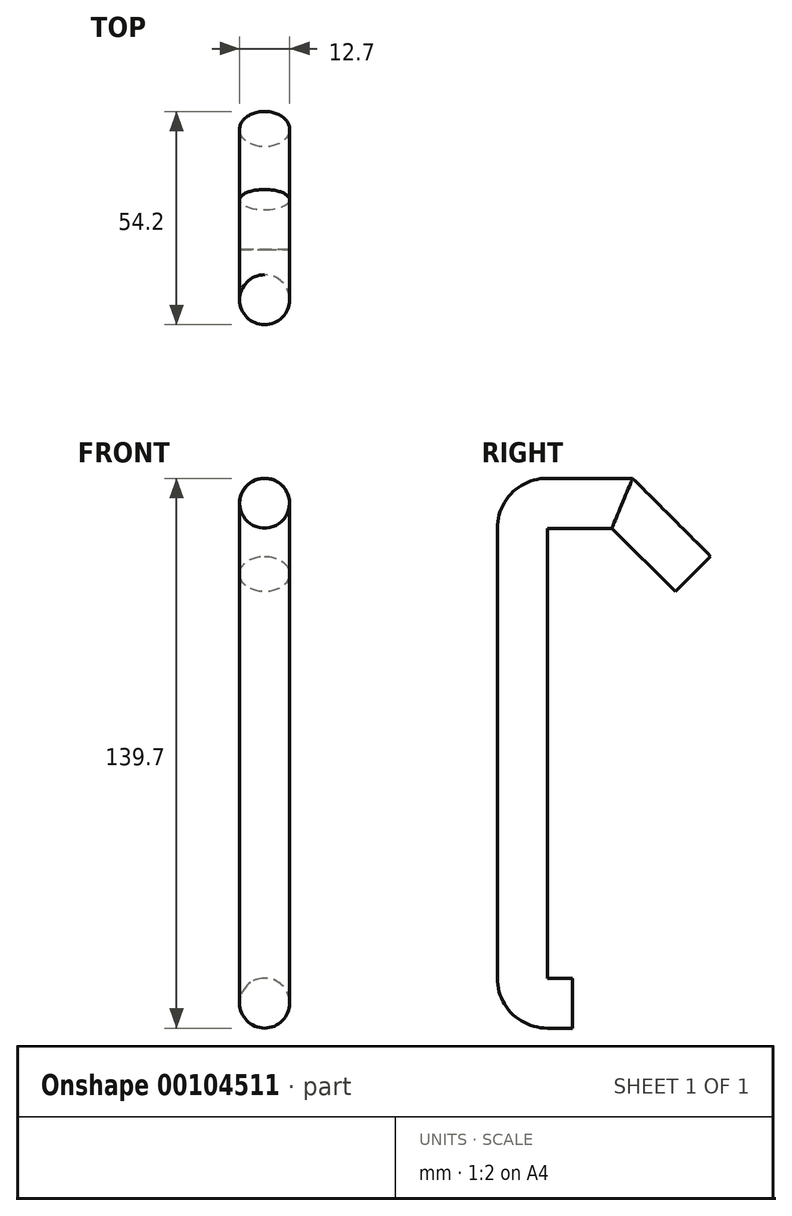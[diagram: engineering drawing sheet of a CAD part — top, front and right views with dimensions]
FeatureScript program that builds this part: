
annotation { "Feature Type Name" : "Feature", "Feature Type Description" : "" }
export const myFeature = defineFeature(function(context is Context, id is Id, definition is map)
    precondition{}
    {
        {
            var Q0;
            Q0=qCreatedBy(makeId("Front.planeOp"),FACE);
            var sketch = newSketch(context, id + "F0", { "sketchPlane" : qUnion([Q0])});
            skCircle(sketch, "E0", {"center": v(0, 0) * mm, "radius": 6.35 * mm});
            skSolve(sketch);
        }
        {
            var Q0;
            Q0=qCreatedBy(makeId("Right.planeOp"),FACE);
            var sketch = newSketch(context, id + "F1", { "sketchPlane" : qUnion([Q0])});
            skPoint(sketch, "E1", {"position": v(-12.7, 127) * mm});
            skPoint(sketch, "E2", {"position": v(0, 0) * mm});
            skPoint(sketch, "E3", {"position": v(-12.7, 0) * mm});
            skLineSegment(sketch, "E4", {"start": v(0, 0) * mm, "end": v(-6.35, 0) * mm});
            skLineSegment(sketch, "E5", {"start": v(-12.7, 120.65) * mm, "end": v(-12.7, 6.35) * mm});
            skArc(sketch, "E6.filletArc", {"start": v(-12.7, 6.35) * mm, "mid": v(-10.84, 1.86) * mm, "end": v(-6.35, 0) * mm});
            skPoint(sketch, "E7", {"position": v(12.7, 127) * mm});
            skLineSegment(sketch, "E8", {"start": v(12.7, 127) * mm, "end": v(-6.35, 127) * mm});
            skArc(sketch, "E9.filletArc", {"start": v(-6.35, 127) * mm, "mid": v(-10.84, 125.14) * mm, "end": v(-12.7, 120.65) * mm});
            skLineSegment(sketch, "E10", {"start": v(12.7, 127) * mm, "end": v(30.66, 109.04) * mm});
            skSolve(sketch);
        }
        {
            var Q0;
            Q0=makeQuery(id+"F0.imprint","IMPRINT",FACE,{"disambiguationData":[TD([[makeQuery(id+"F0.imprint","IMPRINT",EDGE,{"derivedFrom":sQuery(id+"F0.wireOp",EDGE,"E0")}),1.0]])]});
            var Q1;
            Q1=sQuery(id+"F1.wireOp",EDGE,"E4");
            var Q2;
            Q2=sQuery(id+"F1.wireOp",EDGE,"E6.filletArc");
            var Q3;
            Q3=sQuery(id+"F1.wireOp",EDGE,"E5");
            var Q4;
            Q4=sQuery(id+"F1.wireOp",EDGE,"E9.filletArc");
            var Q5;
            Q5=sQuery(id+"F1.wireOp",EDGE,"E8");
            var Q6;
            Q6=sQuery(id+"F1.wireOp",EDGE,"E10");
            sweep(context, id + "F2", {"profiles" : qUnion([Q0]), "path" : qUnion([Q1, Q2, Q3, Q4, Q5, Q6])});
        }
    });
